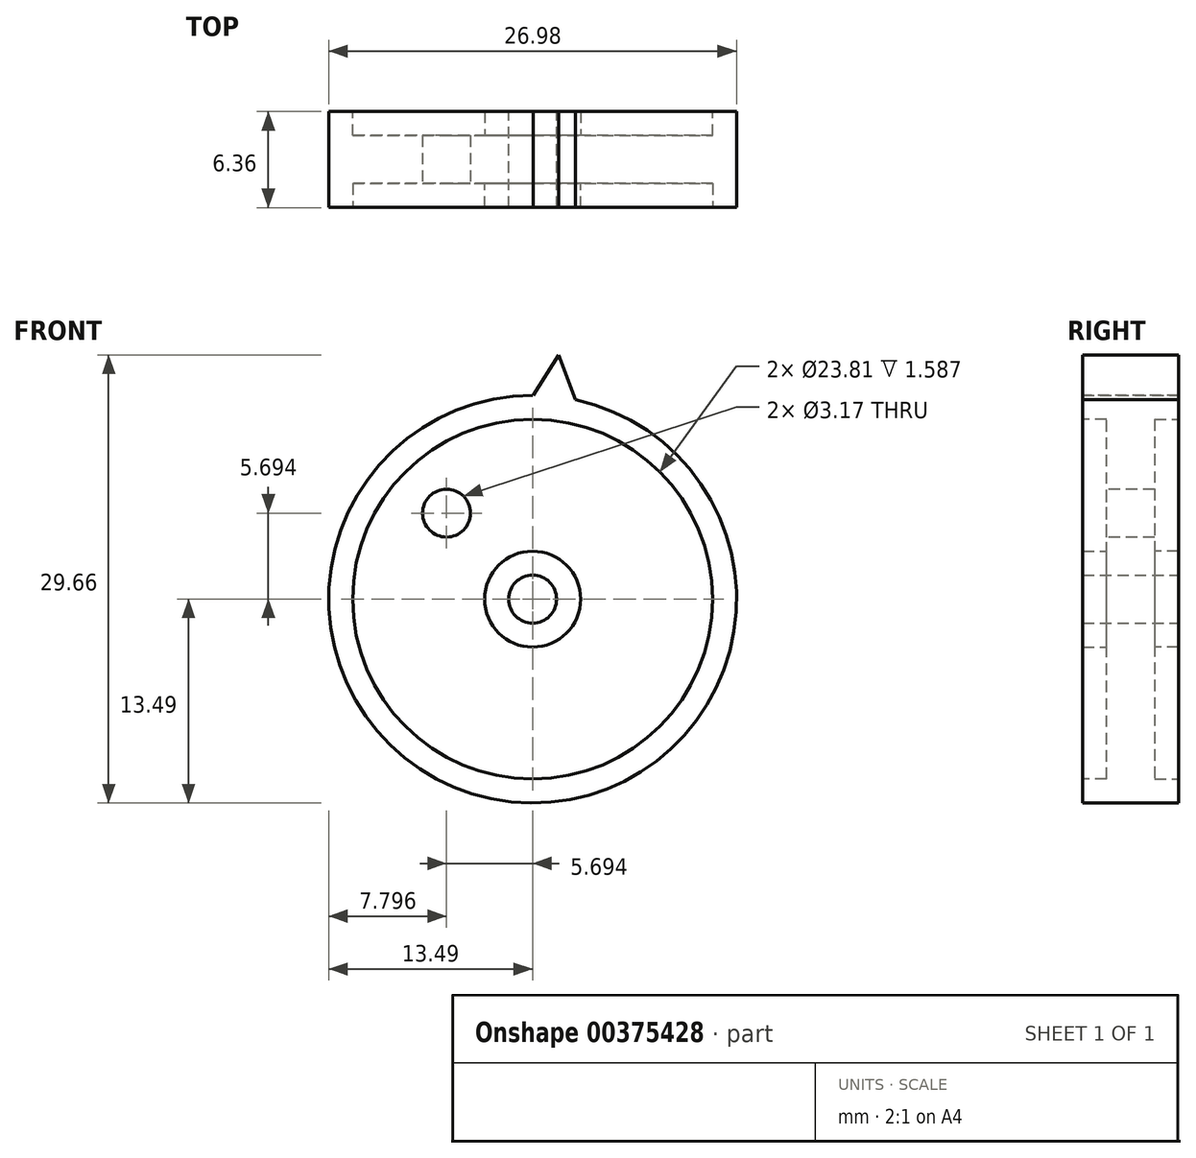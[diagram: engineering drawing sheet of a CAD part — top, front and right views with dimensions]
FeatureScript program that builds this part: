
annotation { "Feature Type Name" : "Feature", "Feature Type Description" : "" }
export const myFeature = defineFeature(function(context is Context, id is Id, definition is map)
    precondition{}
    {
        {
            var Q0;
            Q0=qCreatedBy(makeId("Front.planeOp"),FACE);
            var sketch = newSketch(context, id + "F0", { "sketchPlane" : qUnion([Q0])});
            skCircle(sketch, "E0", {"center": v(0, 0) * mm, "radius": 13.5 * mm});
            skSolve(sketch);
        }
        {
            var Q0;
            Q0=qSketchRegion(id+"F0",true);
            extrude(context, id + "F1", {"entities" : qUnion([Q0]), "depth" : 6.35 * mm, "symmetric" : true});
        }
        {
            var Q0;
            Q0=makeQuery(id+"F1.opExtrude","CAP_FACE",FACE,{"disambiguationData":[OSD([sQuery(id+"F0.wireOp",EDGE,"E0")])],"isStart":false});
            var sketch = newSketch(context, id + "F2", { "sketchPlane" : qUnion([Q0])});
            skLineSegment(sketch, "E1", {"start": v(0.02, 13.5) * mm, "end": v(1.73, 16.17) * mm});
            skLineSegment(sketch, "E2", {"start": v(1.73, 16.17) * mm, "end": v(2.83, 13.2) * mm});
            skLineSegment(sketch, "E3", {"start": v(0, 0) * mm, "end": v(0.02, 13.5) * mm, "construction": true});
            skLineSegment(sketch, "E4", {"start": v(0, 0) * mm, "end": v(2.83, 13.2) * mm, "construction": true});
            skArc(sketch, "E5.0", {"start": v(2.83, 13.2) * mm, "mid": v(1.43, 13.42) * mm, "end": v(0.02, 13.5) * mm});
            skSolve(sketch);
        }
        {
            var Q0;
            Q0=qSketchRegion(id+"F2",true);
            extrude(context, id + "F3", {"entities" : qUnion([Q0]), "operationType" : NewBodyOperationType.ADD, "oppositeDirection" : true, "depth" : 6.35 * mm});
        }
        {
            var Q0;
            {var subQ0=sQuery(id+"F2.wireOp",EDGE,"E5.0");var subQ1=sQuery(id+"F2.wireOp",EDGE,"E2");var subQ2=sQuery(id+"F2.wireOp",EDGE,"E1");Q0=makeQuery(id+"Fj7QE7v1GZ9bRCr_1.29.F3.boolean.opBoolean","MERGE",FACE,{"derivedFrom":[makeQuery(id+"Fj7QE7v1GZ9bRCr_1.28.F3.boolean.opBoolean","MERGE",FACE,{"derivedFrom":[makeQuery(id+"Fj7QE7v1GZ9bRCr_1.27.F3.boolean.opBoolean","MERGE",FACE,{"derivedFrom":[makeQuery(id+"Fj7QE7v1GZ9bRCr_1.26.F3.boolean.opBoolean","MERGE",FACE,{"derivedFrom":[makeQuery(id+"Fj7QE7v1GZ9bRCr_1.25.F3.boolean.opBoolean","MERGE",FACE,{"derivedFrom":[makeQuery(id+"Fj7QE7v1GZ9bRCr_1.24.F3.boolean.opBoolean","MERGE",FACE,{"derivedFrom":[makeQuery(id+"Fj7QE7v1GZ9bRCr_1.23.F3.boolean.opBoolean","MERGE",FACE,{"derivedFrom":[makeQuery(id+"Fj7QE7v1GZ9bRCr_1.22.F3.boolean.opBoolean","MERGE",FACE,{"derivedFrom":[makeQuery(id+"Fj7QE7v1GZ9bRCr_1.21.F3.boolean.opBoolean","MERGE",FACE,{"derivedFrom":[makeQuery(id+"Fj7QE7v1GZ9bRCr_1.20.F3.boolean.opBoolean","MERGE",FACE,{"derivedFrom":[makeQuery(id+"Fj7QE7v1GZ9bRCr_1.19.F3.boolean.opBoolean","MERGE",FACE,{"derivedFrom":[makeQuery(id+"Fj7QE7v1GZ9bRCr_1.18.F3.boolean.opBoolean","MERGE",FACE,{"derivedFrom":[makeQuery(id+"Fj7QE7v1GZ9bRCr_1.17.F3.boolean.opBoolean","MERGE",FACE,{"derivedFrom":[makeQuery(id+"Fj7QE7v1GZ9bRCr_1.16.F3.boolean.opBoolean","MERGE",FACE,{"derivedFrom":[makeQuery(id+"Fj7QE7v1GZ9bRCr_1.15.F3.boolean.opBoolean","MERGE",FACE,{"derivedFrom":[makeQuery(id+"Fj7QE7v1GZ9bRCr_1.14.F3.boolean.opBoolean","MERGE",FACE,{"derivedFrom":[makeQuery(id+"Fj7QE7v1GZ9bRCr_1.13.F3.boolean.opBoolean","MERGE",FACE,{"derivedFrom":[makeQuery(id+"Fj7QE7v1GZ9bRCr_1.12.F3.boolean.opBoolean","MERGE",FACE,{"derivedFrom":[makeQuery(id+"Fj7QE7v1GZ9bRCr_1.11.F3.boolean.opBoolean","MERGE",FACE,{"derivedFrom":[makeQuery(id+"Fj7QE7v1GZ9bRCr_1.10.F3.boolean.opBoolean","MERGE",FACE,{"derivedFrom":[makeQuery(id+"Fj7QE7v1GZ9bRCr_1.9.F3.boolean.opBoolean","MERGE",FACE,{"derivedFrom":[makeQuery(id+"Fj7QE7v1GZ9bRCr_1.8.F3.boolean.opBoolean","MERGE",FACE,{"derivedFrom":[makeQuery(id+"Fj7QE7v1GZ9bRCr_1.7.F3.boolean.opBoolean","MERGE",FACE,{"derivedFrom":[makeQuery(id+"Fj7QE7v1GZ9bRCr_1.6.F3.boolean.opBoolean","MERGE",FACE,{"derivedFrom":[makeQuery(id+"Fj7QE7v1GZ9bRCr_1.5.F3.boolean.opBoolean","MERGE",FACE,{"derivedFrom":[makeQuery(id+"Fj7QE7v1GZ9bRCr_1.4.F3.boolean.opBoolean","MERGE",FACE,{"derivedFrom":[makeQuery(id+"Fj7QE7v1GZ9bRCr_1.3.F3.boolean.opBoolean","MERGE",FACE,{"derivedFrom":[makeQuery(id+"Fj7QE7v1GZ9bRCr_1.2.F3.boolean.opBoolean","MERGE",FACE,{"derivedFrom":[makeQuery(id+"Fj7QE7v1GZ9bRCr_1.1.F3.boolean.opBoolean","MERGE",FACE,{"derivedFrom":[makeQuery(id+"F3.boolean.opBoolean","MERGE",FACE,{"derivedFrom":[makeQuery(id+"F1.opExtrude","CAP_FACE",FACE,{"disambiguationData":[OSD([sQuery(id+"F0.wireOp",EDGE,"E0")])],"isStart":false}),makeQuery(id+"F3.opExtrude","CAP_FACE",FACE,{"disambiguationData":[OSD([subQ2,subQ1,subQ0])],"isStart":true})]}),makeQuery(id+"Fj7QE7v1GZ9bRCr_1.1.F3.opExtrude","CAP_FACE",FACE,{"disambiguationData":[OSD([subQ2,subQ1,subQ0])],"isStart":true})]}),makeQuery(id+"Fj7QE7v1GZ9bRCr_1.2.F3.opExtrude","CAP_FACE",FACE,{"disambiguationData":[OSD([subQ2,subQ1,subQ0])],"isStart":true})]}),makeQuery(id+"Fj7QE7v1GZ9bRCr_1.3.F3.opExtrude","CAP_FACE",FACE,{"disambiguationData":[OSD([subQ2,subQ1,subQ0])],"isStart":true})]}),makeQuery(id+"Fj7QE7v1GZ9bRCr_1.4.F3.opExtrude","CAP_FACE",FACE,{"disambiguationData":[OSD([subQ2,subQ1,subQ0])],"isStart":true})]}),makeQuery(id+"Fj7QE7v1GZ9bRCr_1.5.F3.opExtrude","CAP_FACE",FACE,{"disambiguationData":[OSD([subQ2,subQ1,subQ0])],"isStart":true})]}),makeQuery(id+"Fj7QE7v1GZ9bRCr_1.6.F3.opExtrude","CAP_FACE",FACE,{"disambiguationData":[OSD([subQ2,subQ1,subQ0])],"isStart":true})]}),makeQuery(id+"Fj7QE7v1GZ9bRCr_1.7.F3.opExtrude","CAP_FACE",FACE,{"disambiguationData":[OSD([subQ2,subQ1,subQ0])],"isStart":true})]}),makeQuery(id+"Fj7QE7v1GZ9bRCr_1.8.F3.opExtrude","CAP_FACE",FACE,{"disambiguationData":[OSD([subQ2,subQ1,subQ0])],"isStart":true})]}),makeQuery(id+"Fj7QE7v1GZ9bRCr_1.9.F3.opExtrude","CAP_FACE",FACE,{"disambiguationData":[OSD([subQ2,subQ1,subQ0])],"isStart":true})]}),makeQuery(id+"Fj7QE7v1GZ9bRCr_1.10.F3.opExtrude","CAP_FACE",FACE,{"disambiguationData":[OSD([subQ2,subQ1,subQ0])],"isStart":true})]}),makeQuery(id+"Fj7QE7v1GZ9bRCr_1.11.F3.opExtrude","CAP_FACE",FACE,{"disambiguationData":[OSD([subQ2,subQ1,subQ0])],"isStart":true})]}),makeQuery(id+"Fj7QE7v1GZ9bRCr_1.12.F3.opExtrude","CAP_FACE",FACE,{"disambiguationData":[OSD([subQ2,subQ1,subQ0])],"isStart":true})]}),makeQuery(id+"Fj7QE7v1GZ9bRCr_1.13.F3.opExtrude","CAP_FACE",FACE,{"disambiguationData":[OSD([subQ2,subQ1,subQ0])],"isStart":true})]}),makeQuery(id+"Fj7QE7v1GZ9bRCr_1.14.F3.opExtrude","CAP_FACE",FACE,{"disambiguationData":[OSD([subQ2,subQ1,subQ0])],"isStart":true})]}),makeQuery(id+"Fj7QE7v1GZ9bRCr_1.15.F3.opExtrude","CAP_FACE",FACE,{"disambiguationData":[OSD([subQ2,subQ1,subQ0])],"isStart":true})]}),makeQuery(id+"Fj7QE7v1GZ9bRCr_1.16.F3.opExtrude","CAP_FACE",FACE,{"disambiguationData":[OSD([subQ2,subQ1,subQ0])],"isStart":true})]}),makeQuery(id+"Fj7QE7v1GZ9bRCr_1.17.F3.opExtrude","CAP_FACE",FACE,{"disambiguationData":[OSD([subQ2,subQ1,subQ0])],"isStart":true})]}),makeQuery(id+"Fj7QE7v1GZ9bRCr_1.18.F3.opExtrude","CAP_FACE",FACE,{"disambiguationData":[OSD([subQ2,subQ1,subQ0])],"isStart":true})]}),makeQuery(id+"Fj7QE7v1GZ9bRCr_1.19.F3.opExtrude","CAP_FACE",FACE,{"disambiguationData":[OSD([subQ2,subQ1,subQ0])],"isStart":true})]}),makeQuery(id+"Fj7QE7v1GZ9bRCr_1.20.F3.opExtrude","CAP_FACE",FACE,{"disambiguationData":[OSD([subQ2,subQ1,subQ0])],"isStart":true})]}),makeQuery(id+"Fj7QE7v1GZ9bRCr_1.21.F3.opExtrude","CAP_FACE",FACE,{"disambiguationData":[OSD([subQ2,subQ1,subQ0])],"isStart":true})]}),makeQuery(id+"Fj7QE7v1GZ9bRCr_1.22.F3.opExtrude","CAP_FACE",FACE,{"disambiguationData":[OSD([subQ2,subQ1,subQ0])],"isStart":true})]}),makeQuery(id+"Fj7QE7v1GZ9bRCr_1.23.F3.opExtrude","CAP_FACE",FACE,{"disambiguationData":[OSD([subQ2,subQ1,subQ0])],"isStart":true})]}),makeQuery(id+"Fj7QE7v1GZ9bRCr_1.24.F3.opExtrude","CAP_FACE",FACE,{"disambiguationData":[OSD([subQ2,subQ1,subQ0])],"isStart":true})]}),makeQuery(id+"Fj7QE7v1GZ9bRCr_1.25.F3.opExtrude","CAP_FACE",FACE,{"disambiguationData":[OSD([subQ2,subQ1,subQ0])],"isStart":true})]}),makeQuery(id+"Fj7QE7v1GZ9bRCr_1.26.F3.opExtrude","CAP_FACE",FACE,{"disambiguationData":[OSD([subQ2,subQ1,subQ0])],"isStart":true})]}),makeQuery(id+"Fj7QE7v1GZ9bRCr_1.27.F3.opExtrude","CAP_FACE",FACE,{"disambiguationData":[OSD([subQ2,subQ1,subQ0])],"isStart":true})]}),makeQuery(id+"Fj7QE7v1GZ9bRCr_1.28.F3.opExtrude","CAP_FACE",FACE,{"disambiguationData":[OSD([subQ2,subQ1,subQ0])],"isStart":true})]}),makeQuery(id+"Fj7QE7v1GZ9bRCr_1.29.F3.opExtrude","CAP_FACE",FACE,{"disambiguationData":[OSD([subQ2,subQ1,subQ0])],"isStart":true})]});}
            var sketch = newSketch(context, id + "F4", { "sketchPlane" : qUnion([Q0])});
            skCircle(sketch, "E6", {"center": v(0, 0) * mm, "radius": 11.9 * mm});
            skSolve(sketch);
        }
        {
            var Q0;
            Q0=qSketchRegion(id+"F4",true);
            extrude(context, id + "F5", {"entities" : qUnion([Q0]), "operationType" : NewBodyOperationType.REMOVE, "oppositeDirection" : true, "depth" : 1.59 * mm});
        }
        {
            var Q0;
            {var subQ0=sQuery(id+"F2.wireOp",EDGE,"E5.0");var subQ1=sQuery(id+"F2.wireOp",EDGE,"E2");var subQ2=sQuery(id+"F2.wireOp",EDGE,"E1");Q0=makeQuery(id+"Fj7QE7v1GZ9bRCr_1.29.F3.boolean.opBoolean","MERGE",FACE,{"derivedFrom":[makeQuery(id+"Fj7QE7v1GZ9bRCr_1.28.F3.boolean.opBoolean","MERGE",FACE,{"derivedFrom":[makeQuery(id+"Fj7QE7v1GZ9bRCr_1.27.F3.boolean.opBoolean","MERGE",FACE,{"derivedFrom":[makeQuery(id+"Fj7QE7v1GZ9bRCr_1.26.F3.boolean.opBoolean","MERGE",FACE,{"derivedFrom":[makeQuery(id+"Fj7QE7v1GZ9bRCr_1.25.F3.boolean.opBoolean","MERGE",FACE,{"derivedFrom":[makeQuery(id+"Fj7QE7v1GZ9bRCr_1.24.F3.boolean.opBoolean","MERGE",FACE,{"derivedFrom":[makeQuery(id+"Fj7QE7v1GZ9bRCr_1.23.F3.boolean.opBoolean","MERGE",FACE,{"derivedFrom":[makeQuery(id+"Fj7QE7v1GZ9bRCr_1.22.F3.boolean.opBoolean","MERGE",FACE,{"derivedFrom":[makeQuery(id+"Fj7QE7v1GZ9bRCr_1.21.F3.boolean.opBoolean","MERGE",FACE,{"derivedFrom":[makeQuery(id+"Fj7QE7v1GZ9bRCr_1.20.F3.boolean.opBoolean","MERGE",FACE,{"derivedFrom":[makeQuery(id+"Fj7QE7v1GZ9bRCr_1.19.F3.boolean.opBoolean","MERGE",FACE,{"derivedFrom":[makeQuery(id+"Fj7QE7v1GZ9bRCr_1.18.F3.boolean.opBoolean","MERGE",FACE,{"derivedFrom":[makeQuery(id+"Fj7QE7v1GZ9bRCr_1.17.F3.boolean.opBoolean","MERGE",FACE,{"derivedFrom":[makeQuery(id+"Fj7QE7v1GZ9bRCr_1.16.F3.boolean.opBoolean","MERGE",FACE,{"derivedFrom":[makeQuery(id+"Fj7QE7v1GZ9bRCr_1.15.F3.boolean.opBoolean","MERGE",FACE,{"derivedFrom":[makeQuery(id+"Fj7QE7v1GZ9bRCr_1.14.F3.boolean.opBoolean","MERGE",FACE,{"derivedFrom":[makeQuery(id+"Fj7QE7v1GZ9bRCr_1.13.F3.boolean.opBoolean","MERGE",FACE,{"derivedFrom":[makeQuery(id+"Fj7QE7v1GZ9bRCr_1.12.F3.boolean.opBoolean","MERGE",FACE,{"derivedFrom":[makeQuery(id+"Fj7QE7v1GZ9bRCr_1.11.F3.boolean.opBoolean","MERGE",FACE,{"derivedFrom":[makeQuery(id+"Fj7QE7v1GZ9bRCr_1.10.F3.boolean.opBoolean","MERGE",FACE,{"derivedFrom":[makeQuery(id+"Fj7QE7v1GZ9bRCr_1.9.F3.boolean.opBoolean","MERGE",FACE,{"derivedFrom":[makeQuery(id+"Fj7QE7v1GZ9bRCr_1.8.F3.boolean.opBoolean","MERGE",FACE,{"derivedFrom":[makeQuery(id+"Fj7QE7v1GZ9bRCr_1.7.F3.boolean.opBoolean","MERGE",FACE,{"derivedFrom":[makeQuery(id+"Fj7QE7v1GZ9bRCr_1.6.F3.boolean.opBoolean","MERGE",FACE,{"derivedFrom":[makeQuery(id+"Fj7QE7v1GZ9bRCr_1.5.F3.boolean.opBoolean","MERGE",FACE,{"derivedFrom":[makeQuery(id+"Fj7QE7v1GZ9bRCr_1.4.F3.boolean.opBoolean","MERGE",FACE,{"derivedFrom":[makeQuery(id+"Fj7QE7v1GZ9bRCr_1.3.F3.boolean.opBoolean","MERGE",FACE,{"derivedFrom":[makeQuery(id+"Fj7QE7v1GZ9bRCr_1.2.F3.boolean.opBoolean","MERGE",FACE,{"derivedFrom":[makeQuery(id+"Fj7QE7v1GZ9bRCr_1.1.F3.boolean.opBoolean","MERGE",FACE,{"derivedFrom":[makeQuery(id+"F3.boolean.opBoolean","MERGE",FACE,{"derivedFrom":[makeQuery(id+"F1.opExtrude","CAP_FACE",FACE,{"disambiguationData":[OSD([sQuery(id+"F0.wireOp",EDGE,"E0")])],"isStart":true}),makeQuery(id+"F3.opExtrude","CAP_FACE",FACE,{"disambiguationData":[OSD([subQ2,subQ1,subQ0])],"isStart":false})]}),makeQuery(id+"Fj7QE7v1GZ9bRCr_1.1.F3.opExtrude","CAP_FACE",FACE,{"disambiguationData":[OSD([subQ2,subQ1,subQ0])],"isStart":false})]}),makeQuery(id+"Fj7QE7v1GZ9bRCr_1.2.F3.opExtrude","CAP_FACE",FACE,{"disambiguationData":[OSD([subQ2,subQ1,subQ0])],"isStart":false})]}),makeQuery(id+"Fj7QE7v1GZ9bRCr_1.3.F3.opExtrude","CAP_FACE",FACE,{"disambiguationData":[OSD([subQ2,subQ1,subQ0])],"isStart":false})]}),makeQuery(id+"Fj7QE7v1GZ9bRCr_1.4.F3.opExtrude","CAP_FACE",FACE,{"disambiguationData":[OSD([subQ2,subQ1,subQ0])],"isStart":false})]}),makeQuery(id+"Fj7QE7v1GZ9bRCr_1.5.F3.opExtrude","CAP_FACE",FACE,{"disambiguationData":[OSD([subQ2,subQ1,subQ0])],"isStart":false})]}),makeQuery(id+"Fj7QE7v1GZ9bRCr_1.6.F3.opExtrude","CAP_FACE",FACE,{"disambiguationData":[OSD([subQ2,subQ1,subQ0])],"isStart":false})]}),makeQuery(id+"Fj7QE7v1GZ9bRCr_1.7.F3.opExtrude","CAP_FACE",FACE,{"disambiguationData":[OSD([subQ2,subQ1,subQ0])],"isStart":false})]}),makeQuery(id+"Fj7QE7v1GZ9bRCr_1.8.F3.opExtrude","CAP_FACE",FACE,{"disambiguationData":[OSD([subQ2,subQ1,subQ0])],"isStart":false})]}),makeQuery(id+"Fj7QE7v1GZ9bRCr_1.9.F3.opExtrude","CAP_FACE",FACE,{"disambiguationData":[OSD([subQ2,subQ1,subQ0])],"isStart":false})]}),makeQuery(id+"Fj7QE7v1GZ9bRCr_1.10.F3.opExtrude","CAP_FACE",FACE,{"disambiguationData":[OSD([subQ2,subQ1,subQ0])],"isStart":false})]}),makeQuery(id+"Fj7QE7v1GZ9bRCr_1.11.F3.opExtrude","CAP_FACE",FACE,{"disambiguationData":[OSD([subQ2,subQ1,subQ0])],"isStart":false})]}),makeQuery(id+"Fj7QE7v1GZ9bRCr_1.12.F3.opExtrude","CAP_FACE",FACE,{"disambiguationData":[OSD([subQ2,subQ1,subQ0])],"isStart":false})]}),makeQuery(id+"Fj7QE7v1GZ9bRCr_1.13.F3.opExtrude","CAP_FACE",FACE,{"disambiguationData":[OSD([subQ2,subQ1,subQ0])],"isStart":false})]}),makeQuery(id+"Fj7QE7v1GZ9bRCr_1.14.F3.opExtrude","CAP_FACE",FACE,{"disambiguationData":[OSD([subQ2,subQ1,subQ0])],"isStart":false})]}),makeQuery(id+"Fj7QE7v1GZ9bRCr_1.15.F3.opExtrude","CAP_FACE",FACE,{"disambiguationData":[OSD([subQ2,subQ1,subQ0])],"isStart":false})]}),makeQuery(id+"Fj7QE7v1GZ9bRCr_1.16.F3.opExtrude","CAP_FACE",FACE,{"disambiguationData":[OSD([subQ2,subQ1,subQ0])],"isStart":false})]}),makeQuery(id+"Fj7QE7v1GZ9bRCr_1.17.F3.opExtrude","CAP_FACE",FACE,{"disambiguationData":[OSD([subQ2,subQ1,subQ0])],"isStart":false})]}),makeQuery(id+"Fj7QE7v1GZ9bRCr_1.18.F3.opExtrude","CAP_FACE",FACE,{"disambiguationData":[OSD([subQ2,subQ1,subQ0])],"isStart":false})]}),makeQuery(id+"Fj7QE7v1GZ9bRCr_1.19.F3.opExtrude","CAP_FACE",FACE,{"disambiguationData":[OSD([subQ2,subQ1,subQ0])],"isStart":false})]}),makeQuery(id+"Fj7QE7v1GZ9bRCr_1.20.F3.opExtrude","CAP_FACE",FACE,{"disambiguationData":[OSD([subQ2,subQ1,subQ0])],"isStart":false})]}),makeQuery(id+"Fj7QE7v1GZ9bRCr_1.21.F3.opExtrude","CAP_FACE",FACE,{"disambiguationData":[OSD([subQ2,subQ1,subQ0])],"isStart":false})]}),makeQuery(id+"Fj7QE7v1GZ9bRCr_1.22.F3.opExtrude","CAP_FACE",FACE,{"disambiguationData":[OSD([subQ2,subQ1,subQ0])],"isStart":false})]}),makeQuery(id+"Fj7QE7v1GZ9bRCr_1.23.F3.opExtrude","CAP_FACE",FACE,{"disambiguationData":[OSD([subQ2,subQ1,subQ0])],"isStart":false})]}),makeQuery(id+"Fj7QE7v1GZ9bRCr_1.24.F3.opExtrude","CAP_FACE",FACE,{"disambiguationData":[OSD([subQ2,subQ1,subQ0])],"isStart":false})]}),makeQuery(id+"Fj7QE7v1GZ9bRCr_1.25.F3.opExtrude","CAP_FACE",FACE,{"disambiguationData":[OSD([subQ2,subQ1,subQ0])],"isStart":false})]}),makeQuery(id+"Fj7QE7v1GZ9bRCr_1.26.F3.opExtrude","CAP_FACE",FACE,{"disambiguationData":[OSD([subQ2,subQ1,subQ0])],"isStart":false})]}),makeQuery(id+"Fj7QE7v1GZ9bRCr_1.27.F3.opExtrude","CAP_FACE",FACE,{"disambiguationData":[OSD([subQ2,subQ1,subQ0])],"isStart":false})]}),makeQuery(id+"Fj7QE7v1GZ9bRCr_1.28.F3.opExtrude","CAP_FACE",FACE,{"disambiguationData":[OSD([subQ2,subQ1,subQ0])],"isStart":false})]}),makeQuery(id+"Fj7QE7v1GZ9bRCr_1.29.F3.opExtrude","CAP_FACE",FACE,{"disambiguationData":[OSD([subQ2,subQ1,subQ0])],"isStart":false})]});}
            var sketch = newSketch(context, id + "F6", { "sketchPlane" : qUnion([Q0])});
            skCircle(sketch, "E7.0", {"center": v(0, 0) * mm, "radius": 11.9 * mm});
            skSolve(sketch);
        }
        {
            var Q0;
            Q0=qSketchRegion(id+"F6",true);
            extrude(context, id + "F7", {"entities" : qUnion([Q0]), "operationType" : NewBodyOperationType.REMOVE, "oppositeDirection" : true, "depth" : 1.59 * mm});
        }
        {
            var Q0;
            Q0=makeQuery(id+"F5.boolean.opBoolean","COPY",FACE,{"derivedFrom":makeQuery(id+"F5.opExtrude","CAP_FACE",FACE,{"disambiguationData":[OSD([sQuery(id+"F4.wireOp",EDGE,"E6")])],"isStart":false})});
            var sketch = newSketch(context, id + "F8", { "sketchPlane" : qUnion([Q0])});
            skCircle(sketch, "E8", {"center": v(-5.7, 5.7) * mm, "radius": 1.59 * mm});
            skLineSegment(sketch, "E9", {"start": v(-5.7, 5.7) * mm, "end": v(-5.7, 10.46) * mm, "construction": true});
            skLineSegment(sketch, "E10", {"start": v(-5.7, 10.46) * mm, "end": v(-10.46, 5.7) * mm, "construction": true});
            skLineSegment(sketch, "E11", {"start": v(-10.46, 5.7) * mm, "end": v(-5.7, 5.7) * mm, "construction": true});
            skSolve(sketch);
        }
        {
            var Q0;
            Q0=qSketchRegion(id+"F8",true);
            extrude(context, id + "F9", {"entities" : qUnion([Q0]), "operationType" : NewBodyOperationType.REMOVE, "endBound" : BoundingType.THROUGH_ALL, "oppositeDirection" : true, "depth" : 25.4 * mm});
        }
        {
            var Q0;
            Q0=makeQuery(id+"F5.boolean.opBoolean","COPY",FACE,{"derivedFrom":makeQuery(id+"F5.opExtrude","CAP_FACE",FACE,{"disambiguationData":[OSD([sQuery(id+"F4.wireOp",EDGE,"E6")])],"isStart":false})});
            var sketch = newSketch(context, id + "F10", { "sketchPlane" : qUnion([Q0])});
            skCircle(sketch, "E12", {"center": v(0, 0) * mm, "radius": 3.18 * mm});
            skSolve(sketch);
        }
        {
            var Q0;
            Q0=qSketchRegion(id+"F10",true);
            extrude(context, id + "F11", {"entities" : qUnion([Q0]), "operationType" : NewBodyOperationType.ADD, "depth" : 1.59 * mm});
        }
        {
            var Q0;
            Q0=makeQuery(id+"F7.boolean.opBoolean","COPY",FACE,{"derivedFrom":makeQuery(id+"F7.opExtrude","CAP_FACE",FACE,{"disambiguationData":[OSD([sQuery(id+"F6.wireOp",EDGE,"E7.0")])],"isStart":false})});
            var sketch = newSketch(context, id + "F12", { "sketchPlane" : qUnion([Q0])});
            skCircle(sketch, "E13", {"center": v(0, 0) * mm, "radius": 3.18 * mm});
            skSolve(sketch);
        }
        {
            var Q0;
            Q0=qSketchRegion(id+"F12",true);
            extrude(context, id + "F13", {"entities" : qUnion([Q0]), "operationType" : NewBodyOperationType.ADD, "depth" : 1.59 * mm});
        }
        {
            var Q0;
            Q0=makeQuery(id+"F13.opExtrude","CAP_FACE",FACE,{"disambiguationData":[OSD([sQuery(id+"F12.wireOp",EDGE,"E13")])],"isStart":false});
            var sketch = newSketch(context, id + "F14", { "sketchPlane" : qUnion([Q0])});
            skCircle(sketch, "E14", {"center": v(0, 0) * mm, "radius": 1.59 * mm});
            skSolve(sketch);
        }
        {
            var Q0;
            Q0=qSketchRegion(id+"F14",true);
            extrude(context, id + "F15", {"entities" : qUnion([Q0]), "operationType" : NewBodyOperationType.REMOVE, "endBound" : BoundingType.THROUGH_ALL, "oppositeDirection" : true, "depth" : 25.4 * mm});
        }
    });
